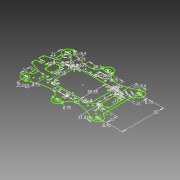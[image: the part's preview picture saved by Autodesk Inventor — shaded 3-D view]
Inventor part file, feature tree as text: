
AUTODESK INVENTOR PART (.ipt)
format: ipt  version: 2012 (Build 160160000, 160)  size: 155,136 bytes
history: native  units: mm
features: sketch x1
ambient origin geometry x8: Origin, YZ Plane, XZ Plane, XY Plane, X Axis, Y Axis, Z Axis, Center Point
feature tree (1):
  sketch  "Sketch1"  dims[d0=2.0mm d1=5.0mm d2=5.0mm d3=3.0mm d4=3.0mm d5=15.0mm d6=15.0mm d7=30.0mm d8=82.0mm d9=2.0mm d10=2.0mm d11=5.0mm d12=10.0mm d13=15.0mm d14=20.0mm d15=2.0mm d16=8.75mm d17=8.75mm d18=8.75mm d19=8.75mm d20=8.75mm d21=8.75mm d22=2.0mm d23=2.0mm d24=9.0mm d25=2.0mm d26=2.0mm d27=9.0mm d28=10.0mm d29=6.0mm d30=21.0mm d31=21.014083mm d32=21.014083mm d33=21.0mm d34=21.0mm d35=21.014083mm d36=21.0mm d37=21.014083mm d38=4.0mm d39=4.0mm d40=4.0mm d41=4.0mm d42=4.0mm d43=4.0mm d44=4.0mm d45=4.0mm d46=4.0mm d47=4.0mm d48=4.0mm d49=4.0mm d50=68.5mm d51=50.55mm d52=15.0mm d53=15.0mm d54=15.0mm d55=15.0mm d56=5.632993mm d57=10.75mm d58=10.0mm d59=10.0mm d60=4.7mm d61=5.0mm d62=5.0mm d63=5.0mm d64=10.8mm d65=10.0mm d66=4.7mm d67=5.0mm d68=5.0mm d69=10.0mm d70=5.0mm d71=5.0mm d72=5.682993mm d73=50.55mm d74=68.5mm d75=3.0mm d76=5.0mm d77=5.0mm]
